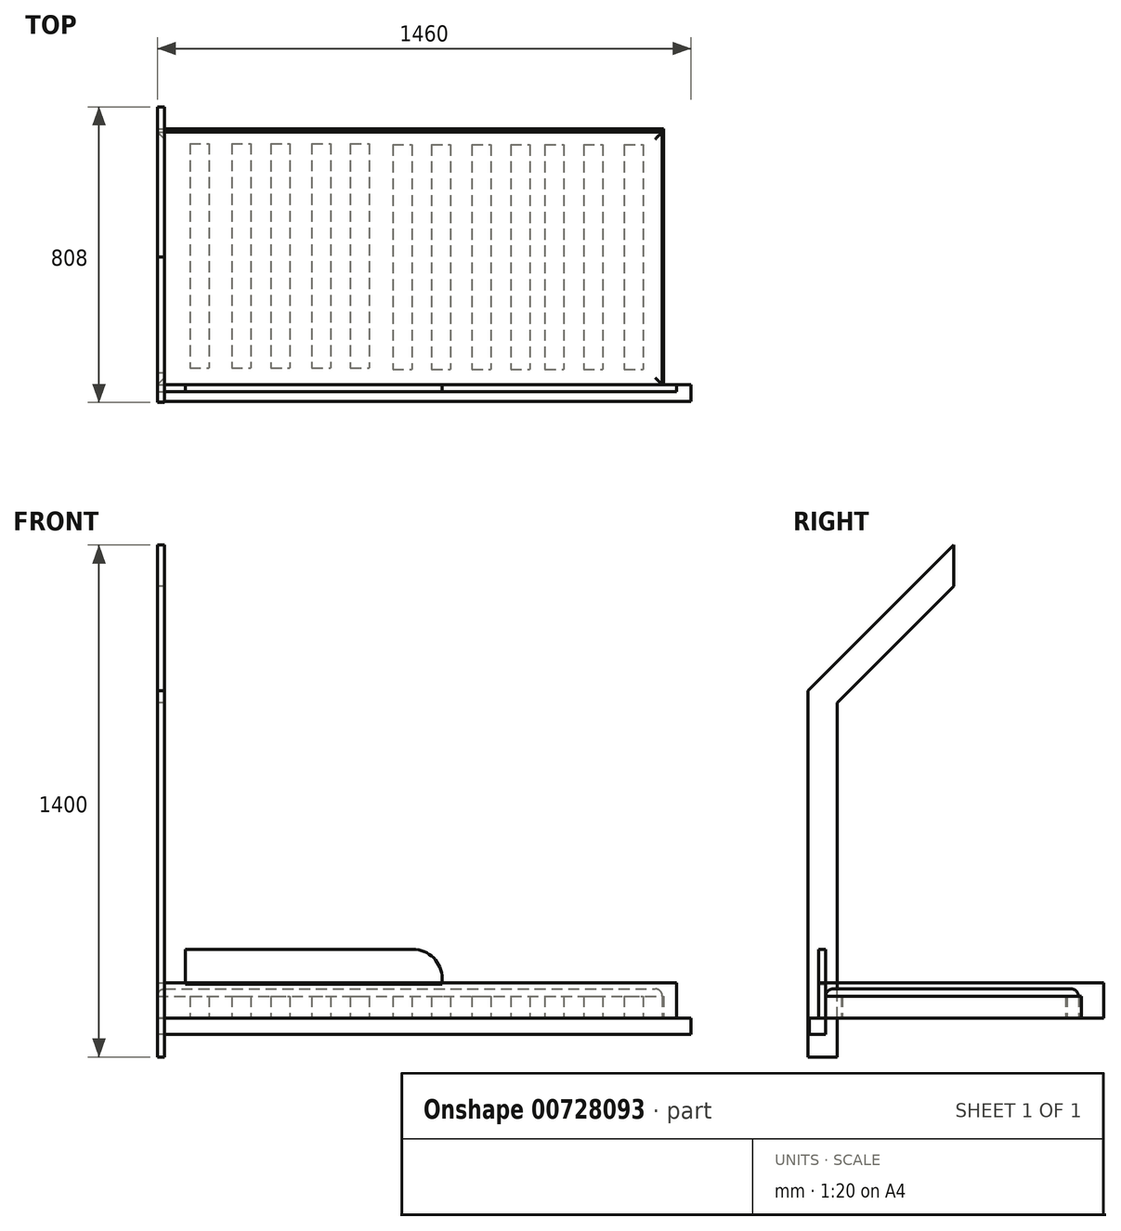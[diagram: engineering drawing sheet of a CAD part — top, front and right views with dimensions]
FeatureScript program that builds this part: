
annotation { "Feature Type Name" : "Feature", "Feature Type Description" : "" }
export const myFeature = defineFeature(function(context is Context, id is Id, definition is map)
    precondition{}
    {
        {
            var Q0;
            Q0=qCreatedBy(makeId("Top.planeOp"),FACE);
            var sketch = newSketch(context, id + "F0", { "sketchPlane" : qUnion([Q0])});
            skLineSegment(sketch, "E0.bottom", {"start": v(0.1, -0.1) * mm, "end": v(1385.1, -0.1) * mm});
            skLineSegment(sketch, "E0.top", {"start": v(0.1, 699.9) * mm, "end": v(1385.1, 699.9) * mm});
            skLineSegment(sketch, "E0.left", {"start": v(0.1, -0.1) * mm, "end": v(0.1, 699.9) * mm});
            skLineSegment(sketch, "E0.right", {"start": v(1385.1, -0.1) * mm, "end": v(1385.1, 699.9) * mm});
            skLineSegment(sketch, "E1.bottom", {"start": v(88.67, 659.99) * mm, "end": v(140.73, 659.99) * mm});
            skLineSegment(sketch, "E1.top", {"start": v(88.67, 45.9) * mm, "end": v(140.73, 45.9) * mm});
            skLineSegment(sketch, "E1.left", {"start": v(88.67, 659.99) * mm, "end": v(88.67, 45.9) * mm});
            skLineSegment(sketch, "E1.right", {"start": v(140.73, 659.99) * mm, "end": v(140.73, 45.9) * mm});
            skLineSegment(sketch, "E2.bottom", {"start": v(527.89, 659.99) * mm, "end": v(579.94, 659.99) * mm});
            skLineSegment(sketch, "E2.top", {"start": v(527.89, 45.9) * mm, "end": v(579.94, 45.9) * mm});
            skLineSegment(sketch, "E2.left", {"start": v(527.89, 659.99) * mm, "end": v(527.89, 45.9) * mm});
            skLineSegment(sketch, "E2.right", {"start": v(579.94, 659.99) * mm, "end": v(579.94, 45.9) * mm});
            skLineSegment(sketch, "E3.bottom", {"start": v(203.2, 660.1) * mm, "end": v(255.26, 660.1) * mm});
            skLineSegment(sketch, "E3.top", {"start": v(203.2, 46) * mm, "end": v(255.26, 46) * mm});
            skLineSegment(sketch, "E3.left", {"start": v(203.2, 660.1) * mm, "end": v(203.2, 46) * mm});
            skLineSegment(sketch, "E3.right", {"start": v(255.26, 660.1) * mm, "end": v(255.26, 46) * mm});
            skLineSegment(sketch, "E4.bottom", {"start": v(422.42, 660.1) * mm, "end": v(474.48, 660.1) * mm});
            skLineSegment(sketch, "E4.top", {"start": v(422.42, 46) * mm, "end": v(474.48, 46) * mm});
            skLineSegment(sketch, "E4.left", {"start": v(422.42, 660.1) * mm, "end": v(422.42, 46) * mm});
            skLineSegment(sketch, "E4.right", {"start": v(474.48, 660.1) * mm, "end": v(474.48, 46) * mm});
            skLineSegment(sketch, "E5.bottom", {"start": v(749.63, 656.86) * mm, "end": v(801.69, 656.86) * mm});
            skLineSegment(sketch, "E5.top", {"start": v(749.63, 42.77) * mm, "end": v(801.69, 42.77) * mm});
            skLineSegment(sketch, "E5.left", {"start": v(749.63, 656.86) * mm, "end": v(749.63, 42.77) * mm});
            skLineSegment(sketch, "E5.right", {"start": v(801.69, 656.86) * mm, "end": v(801.69, 42.77) * mm});
            skLineSegment(sketch, "E6.bottom", {"start": v(643.73, 656.86) * mm, "end": v(695.79, 656.86) * mm});
            skLineSegment(sketch, "E6.top", {"start": v(643.73, 42.77) * mm, "end": v(695.79, 42.77) * mm});
            skLineSegment(sketch, "E6.left", {"start": v(643.73, 656.86) * mm, "end": v(643.73, 42.77) * mm});
            skLineSegment(sketch, "E6.right", {"start": v(695.79, 656.86) * mm, "end": v(695.79, 42.77) * mm});
            skLineSegment(sketch, "E7.bottom", {"start": v(966.25, 656.86) * mm, "end": v(1018.3, 656.86) * mm});
            skLineSegment(sketch, "E7.top", {"start": v(966.25, 42.77) * mm, "end": v(1018.3, 42.77) * mm});
            skLineSegment(sketch, "E7.left", {"start": v(966.25, 656.86) * mm, "end": v(966.25, 42.77) * mm});
            skLineSegment(sketch, "E7.right", {"start": v(1018.3, 656.86) * mm, "end": v(1018.3, 42.77) * mm});
            skLineSegment(sketch, "E8.bottom", {"start": v(860.34, 656.86) * mm, "end": v(912.4, 656.86) * mm});
            skLineSegment(sketch, "E8.top", {"start": v(860.34, 42.77) * mm, "end": v(912.4, 42.77) * mm});
            skLineSegment(sketch, "E8.left", {"start": v(860.34, 656.86) * mm, "end": v(860.34, 42.77) * mm});
            skLineSegment(sketch, "E8.right", {"start": v(912.4, 656.86) * mm, "end": v(912.4, 42.77) * mm});
            skLineSegment(sketch, "E9.bottom", {"start": v(1166, 656.86) * mm, "end": v(1218.05, 656.86) * mm});
            skLineSegment(sketch, "E9.top", {"start": v(1166, 42.77) * mm, "end": v(1218.05, 42.77) * mm});
            skLineSegment(sketch, "E9.left", {"start": v(1166, 656.86) * mm, "end": v(1166, 42.77) * mm});
            skLineSegment(sketch, "E9.right", {"start": v(1218.05, 656.86) * mm, "end": v(1218.05, 42.77) * mm});
            skLineSegment(sketch, "E10.bottom", {"start": v(1060.1, 656.86) * mm, "end": v(1112.15, 656.86) * mm});
            skLineSegment(sketch, "E10.top", {"start": v(1060.1, 42.77) * mm, "end": v(1112.15, 42.77) * mm});
            skLineSegment(sketch, "E10.left", {"start": v(1060.1, 656.86) * mm, "end": v(1060.1, 42.77) * mm});
            skLineSegment(sketch, "E10.right", {"start": v(1112.15, 656.86) * mm, "end": v(1112.15, 42.77) * mm});
            skLineSegment(sketch, "E11.bottom", {"start": v(1276.7, 656.86) * mm, "end": v(1328.77, 656.86) * mm});
            skLineSegment(sketch, "E11.top", {"start": v(1276.7, 42.77) * mm, "end": v(1328.77, 42.77) * mm});
            skLineSegment(sketch, "E11.left", {"start": v(1276.7, 656.86) * mm, "end": v(1276.7, 42.77) * mm});
            skLineSegment(sketch, "E11.right", {"start": v(1328.77, 656.86) * mm, "end": v(1328.77, 42.77) * mm});
            skLineSegment(sketch, "E12.bottom", {"start": v(310.26, 659.99) * mm, "end": v(362.32, 659.99) * mm});
            skLineSegment(sketch, "E12.top", {"start": v(310.26, 45.9) * mm, "end": v(362.32, 45.9) * mm});
            skLineSegment(sketch, "E12.left", {"start": v(310.26, 659.99) * mm, "end": v(310.26, 45.9) * mm});
            skLineSegment(sketch, "E12.right", {"start": v(362.32, 659.99) * mm, "end": v(362.32, 45.9) * mm});
            skSolve(sketch);
        }
        {
            var Q0;
            Q0=makeQuery(id+"F0.imprint","IMPRINT",FACE,{"disambiguationData":[TD([[makeQuery(id+"F0.imprint","IMPRINT",EDGE,{"derivedFrom":sQuery(id+"F0.wireOp",EDGE,"E0.bottom")}),1.0]])]});
            extrude(context, id + "F1", {"entities" : qUnion([Q0]), "depth" : 60 * mm, "offsetDistance" : 25 * mm});
        }
        {
            var Q0;
            Q0=qCreatedBy(makeId("Top.planeOp"),FACE);
            var sketch = newSketch(context, id + "F2", { "sketchPlane" : qUnion([Q0])});
            skLineSegment(sketch, "E13.bottom", {"start": v(-9.9, 21.9) * mm, "end": v(-28.9, 21.9) * mm});
            skLineSegment(sketch, "E13.top", {"start": v(-9.9, -58.1) * mm, "end": v(-28.9, -58.1) * mm});
            skLineSegment(sketch, "E13.left", {"start": v(-9.9, 21.9) * mm, "end": v(-9.9, -58.1) * mm});
            skLineSegment(sketch, "E13.right", {"start": v(-28.9, 21.9) * mm, "end": v(-28.9, -58.1) * mm});
            skSolve(sketch);
        }
        {
            var Q0;
            Q0=qCreatedBy(makeId("Right.planeOp"),FACE);
            var sketch = newSketch(context, id + "F3", { "sketchPlane" : qUnion([Q0])});
            skLineSegment(sketch, "E14", {"start": v(0, 0) * mm, "end": v(0, -106.12) * mm});
            skLineSegment(sketch, "E15", {"start": v(0, -106.12) * mm, "end": v(-10, -106.12) * mm});
            skLineSegment(sketch, "E16", {"start": v(-10, -106.12) * mm, "end": v(-29, -106.12) * mm});
            skLineSegment(sketch, "E17", {"start": v(-29, -106.12) * mm, "end": v(-48, -106.12) * mm});
            skLineSegment(sketch, "E18", {"start": v(-48, -106.12) * mm, "end": v(32, -106.12) * mm});
            skLineSegment(sketch, "E19", {"start": v(350, 0) * mm, "end": v(0, 0) * mm});
            skLineSegment(sketch, "E20", {"start": v(350, 0) * mm, "end": v(350, 1293.88) * mm});
            skLineSegment(sketch, "E21", {"start": v(-48, -106.12) * mm, "end": v(-48, 895.88) * mm});
            skLineSegment(sketch, "E22", {"start": v(-48, 895.88) * mm, "end": v(350, 1293.88) * mm});
            skLineSegment(sketch, "E23", {"start": v(32, -106.12) * mm, "end": v(32, 862.75) * mm});
            skLineSegment(sketch, "E24", {"start": v(32, 862.75) * mm, "end": v(350, 1180.75) * mm});
            skSolve(sketch);
        }
        {
            var Q0;
            {var subQ1=sQuery(id+"F3.wireOp",EDGE,"E14");Q0=makeQuery(id+"F3.imprint","IMPRINT",FACE,{"disambiguationData":[TD([[makeQuery(id+"F3.imprint","IMPRINT",EDGE,{"derivedFrom":subQ1}),-1.0]])]});}
            var Q1;
            {var subQ0=sQuery(id+"F3.wireOp",EDGE,"E14");Q1=makeQuery(id+"F3.imprint","IMPRINT",FACE,{"disambiguationData":[TD([[makeQuery(id+"F3.imprint","IMPRINT",EDGE,{"derivedFrom":subQ0}),1.0]])]});}
            extrude(context, id + "F4", {"entities" : qUnion([Q0, Q1]), "depth" : 19 * mm, "offsetDistance" : 25 * mm});
        }
        {
            var Q0;
            Q0=qCreatedBy(makeId("Right.planeOp"),FACE);
            var sketch = newSketch(context, id + "F5", { "sketchPlane" : qUnion([Q0])});
            skLineSegment(sketch, "E25.bottom", {"start": v(0, 0) * mm, "end": v(760, 0) * mm});
            skLineSegment(sketch, "E25.top", {"start": v(0, 96) * mm, "end": v(760, 96) * mm});
            skLineSegment(sketch, "E25.left", {"start": v(0, 0) * mm, "end": v(0, 96) * mm});
            skLineSegment(sketch, "E25.right", {"start": v(760, 0) * mm, "end": v(760, 96) * mm});
            skSolve(sketch);
        }
        {
            var Q0;
            Q0 = qSketchRegion(id + "F5", true);
            extrude(context, id + "F6", {"entities" : qUnion([Q0]), "depth" : 19 * mm, "offsetDistance" : 25 * mm});
        }
        {
            var Q0;
            Q0=qCreatedBy(makeId("Front.planeOp"),FACE);
            var sketch = newSketch(context, id + "F7", { "sketchPlane" : qUnion([Q0])});
            skLineSegment(sketch, "E26.bottom", {"start": v(0, 0) * mm, "end": v(1420, 0) * mm});
            skLineSegment(sketch, "E26.top", {"start": v(0, 96) * mm, "end": v(1420, 96) * mm});
            skLineSegment(sketch, "E26.left", {"start": v(0, 0) * mm, "end": v(0, 96) * mm});
            skLineSegment(sketch, "E26.right", {"start": v(1420, 0) * mm, "end": v(1420, 96) * mm});
            skSolve(sketch);
        }
        {
            var Q0;
            Q0 = qSketchRegion(id + "F7", true);
            extrude(context, id + "F8", {"entities" : qUnion([Q0]), "depth" : 19 * mm, "offsetDistance" : 25 * mm});
        }
        {
            var Q0;
            Q0=qCreatedBy(makeId("Right.planeOp"),FACE);
            var sketch = newSketch(context, id + "F9", { "sketchPlane" : qUnion([Q0])});
            skLineSegment(sketch, "E27.bottom", {"start": v(0, 0) * mm, "end": v(-45, 0) * mm});
            skLineSegment(sketch, "E27.top", {"start": v(0, -45) * mm, "end": v(-45, -45) * mm});
            skLineSegment(sketch, "E27.left", {"start": v(0, 0) * mm, "end": v(0, -45) * mm});
            skLineSegment(sketch, "E27.right", {"start": v(-45, 0) * mm, "end": v(-45, -45) * mm});
            skSolve(sketch);
        }
        {
            var Q0;
            Q0 = qSketchRegion(id + "F9", true);
            extrude(context, id + "F10", {"entities" : qUnion([Q0]), "depth" : 1460 * mm, "offsetDistance" : 25 * mm});
        }
        {
            var Q0;
            Q0=qCreatedBy(makeId("Front.planeOp"),FACE);
            var sketch = newSketch(context, id + "F11", { "sketchPlane" : qUnion([Q0])});
            skLineSegment(sketch, "E28.bottom", {"start": v(76.52, 188.17) * mm, "end": v(698.92, 188.17) * mm});
            skLineSegment(sketch, "E28.top", {"start": v(76.52, 92.17) * mm, "end": v(778.92, 92.17) * mm});
            skLineSegment(sketch, "E28.left", {"start": v(76.52, 188.17) * mm, "end": v(76.52, 92.17) * mm});
            skLineSegment(sketch, "E28.right", {"start": v(778.92, 108.17) * mm, "end": v(778.92, 92.17) * mm});
            skPoint(sketch, "E29.visualSharp", {"position": v(778.92, 188.17) * mm});
            skArc(sketch, "E29.filletArc", {"start": v(778.92, 108.17) * mm, "mid": v(755.5, 164.74) * mm, "end": v(698.92, 188.17) * mm});
            skSolve(sketch);
        }
        {
            var Q0;
            Q0 = qSketchRegion(id + "F11", true);
            extrude(context, id + "F12", {"entities" : qUnion([Q0]), "depth" : 19 * mm, "offsetDistance" : 25 * mm});
        }
        {
            var Q0;
            Q0=qCreatedBy(makeId("Top.planeOp"),FACE);
            var sketch = newSketch(context, id + "F13", { "sketchPlane" : qUnion([Q0])});
            skLineSegment(sketch, "E30.bottom", {"start": v(0, 0) * mm, "end": v(1381.45, 0) * mm});
            skLineSegment(sketch, "E30.top", {"start": v(0, 691.54) * mm, "end": v(1381.45, 691.54) * mm});
            skLineSegment(sketch, "E30.left", {"start": v(0, 0) * mm, "end": v(0, 691.54) * mm});
            skLineSegment(sketch, "E30.right", {"start": v(1381.45, 0) * mm, "end": v(1381.45, 691.54) * mm});
            skSolve(sketch);
        }
        {
            var Q0;
            Q0 = qSketchRegion(id + "F13", true);
            extrude(context, id + "F14", {"entities" : qUnion([Q0]), "depth" : 80 * mm, "offsetDistance" : 25 * mm});
        }
        {
            var Q0;
            Q0=makeQuery(id+"F14.opExtrude","CAP_FACE",FACE,{"disambiguationData":[OSD([sQuery(id+"F13.wireOp",EDGE,"E30.bottom"),sQuery(id+"F13.wireOp",EDGE,"E30.top"),sQuery(id+"F13.wireOp",EDGE,"E30.left"),sQuery(id+"F13.wireOp",EDGE,"E30.right")])],"isStart":false});
            var Q1;
            Q1=makeQuery(id+"F14.opExtrude","CAP_EDGE",EDGE,{"disambiguationData":[OSD([sQuery(id+"F13.wireOp",EDGE,"E30.right")])],"isStart":false});
            fillet(context, id + "F15", {"entities" : qUnion([Q0, Q1]), "radius" : 20 * mm, "tangentPropagation" : true, "allowEdgeOverflow" : false});
        }
    });
